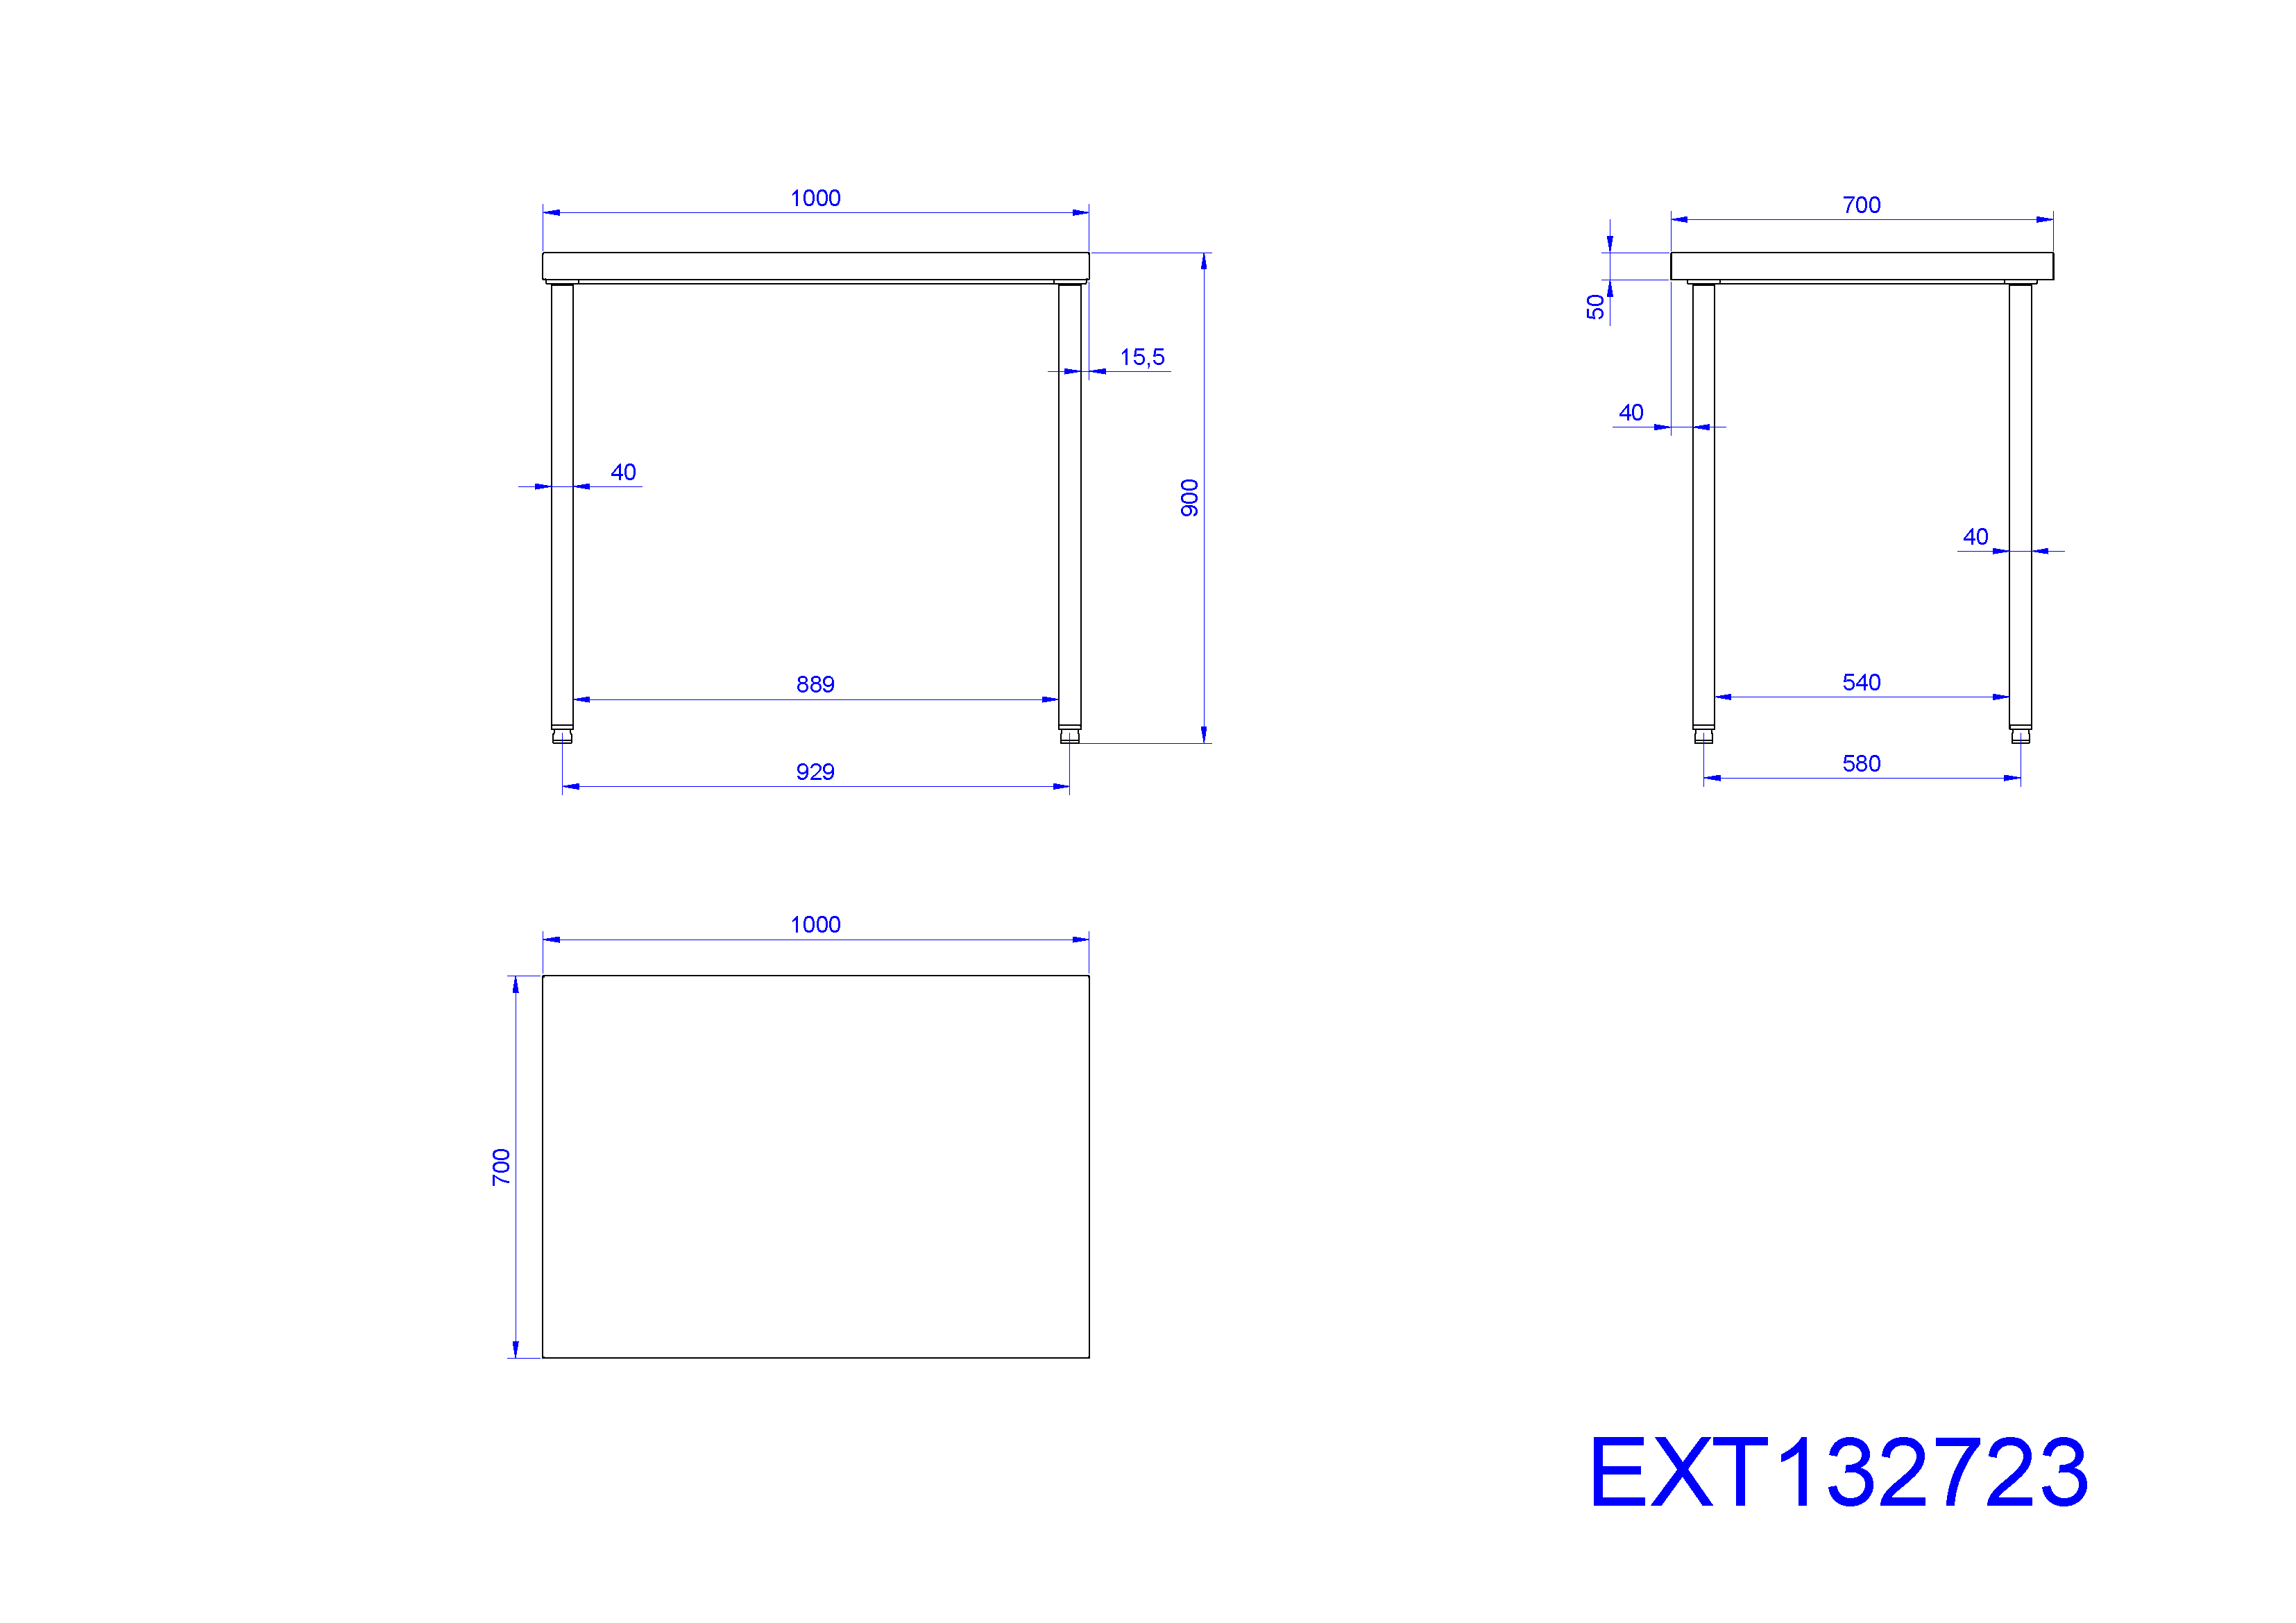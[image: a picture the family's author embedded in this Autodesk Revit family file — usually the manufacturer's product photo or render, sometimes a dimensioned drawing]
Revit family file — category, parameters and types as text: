
# Revit family: QF_ZANUSSI_132728_TG2000PN
name_source: partatom
category: Attrezzature speciali
units: mm (PartAtom-declared; Revit-internal decimal feet)

## family parameters
Basato su piano di lavoro = No
Condiviso = No
Punto di calcolo locali = No
Quota connettore circolare = Usa diametro
Sempre verticale = Sì
Taglio con vuoti quando caricato = No
Tipo di parte = Normale

## types (1)
- Standard
    Accessory = Sì
    Cold Water Size = 0 mm
    Compressed Air Pressure = 0.0 Pa
    Compressed Air Size = 0 mm
    Compressed Air Volume = 0.0 L/s
    Condensate Return Size = 0 mm
    Cycle = 0 Hz
    Depth Actual = 700 mm  [stored 2.29659 ft]
    Descrizione = WORK TABLE 2000 MM
    Direct Waste Size = 0 mm
    Gas Input Pressure = 0
    Gas KW = 0
    Gas Size = 0 mm
    HP = 0 HP
    Height Actual = 900 mm  [stored 2.95276 ft]
    Hot Water Size = 0 mm
    Item Number = 132728
    Length Actual = 2000 mm  [stored 6.56168 ft]
    Modello = TG2000PN
    Phase = 0
    Produttore = Zanussi
    Prospetto di default = 0 mm  [stored 0 ft]
    Refrigerant Compressor Remote = Sì
    Refrigeration Liquid Line Size = 0 mm  [stored 0 ft]
    Refrigeration Suction Line Size = 0 mm  [stored 0 ft]
    Steam Consumption per Hour = 0
    Steam Supply Maximum Pressure = 0.0 Pa
    Steam Supply Minimum Pressure = 0.0 Pa
    Steam Supply Size = 0 mm
    URL = http://www.zanussiprofessional.com
    URL Manufacturer = http://www.zanussiprofessional.com
    Volts = 0 V
    Watts = 0 W
    Weight = 58.00 kg

note: source unit labels omitted for Gas Input Pressure — the stored unit's dimension contradicts the parameter name (converter mislabeling)

note: [stored X ft] marks values corroborated as IEEE doubles in the binary element streams (Revit-internal decimal feet)

## geometry (parser evidence)
native form markers: Sweep x2
no freeform markers — native parametric forms only
